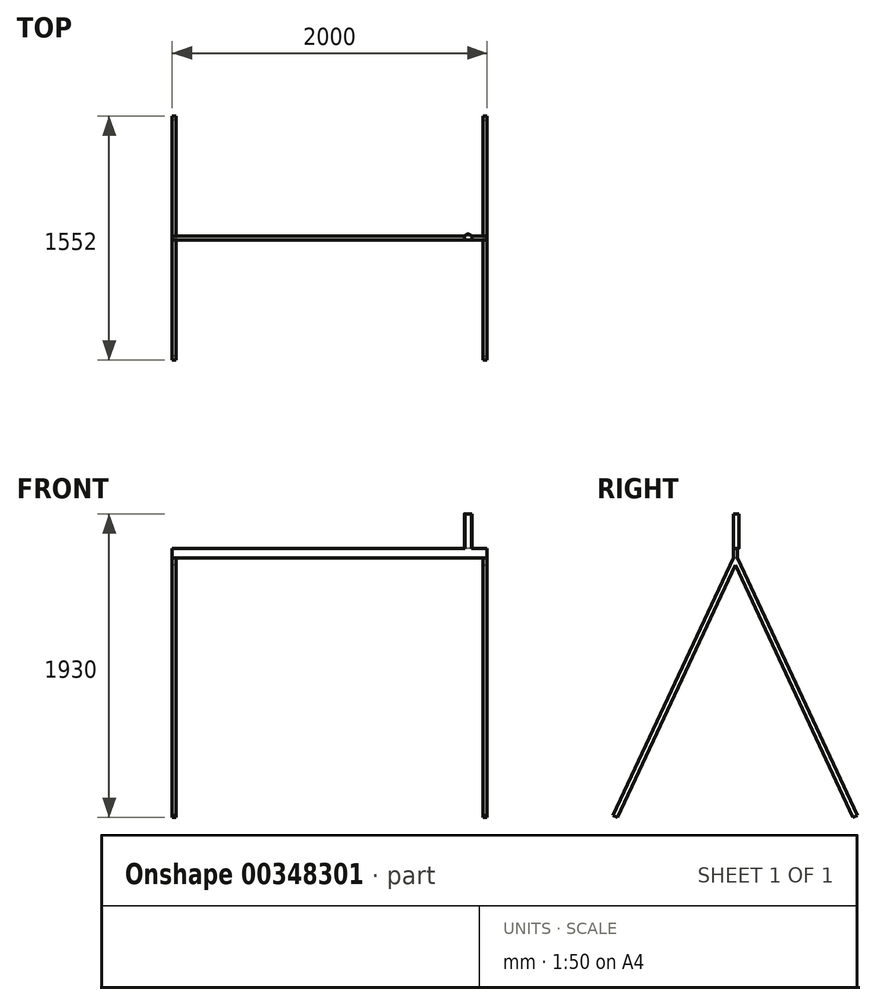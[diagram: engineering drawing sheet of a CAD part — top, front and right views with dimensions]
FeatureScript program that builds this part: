
annotation { "Feature Type Name" : "Feature", "Feature Type Description" : "" }
export const myFeature = defineFeature(function(context is Context, id is Id, definition is map)
    precondition{}
    {
        {
            var Q0;
            Q0=qCreatedBy(makeId("Right.planeOp"),FACE);
            var sketch = newSketch(context, id + "F0", { "sketchPlane" : qUnion([Q0])});
            skLineSegment(sketch, "E0.bottom", {"start": v(12.5, 1710) * mm, "end": v(-12.5, 1710) * mm});
            skLineSegment(sketch, "E0.top", {"start": v(12.5, 1650) * mm, "end": v(-12.5, 1650) * mm});
            skLineSegment(sketch, "E0.left", {"start": v(12.5, 1710) * mm, "end": v(12.5, 1650) * mm});
            skLineSegment(sketch, "E0.right", {"start": v(-12.5, 1710) * mm, "end": v(-12.5, 1650) * mm});
            skPoint(sketch, "E0.middle", {"position": v(0, 1680) * mm});
            skSolve(sketch);
        }
        {
            var Q0;
            Q0 = qSketchRegion(id + "F0", true);
            extrude(context, id + "F1", {"entities" : qUnion([Q0]), "depth" : 2000 * mm, "symmetric" : true});
        }
        {
            var Q0;
            Q0=makeQuery(id+"F1.opExtrude","CAP_FACE",FACE,{"disambiguationData":[OSD([sQuery(id+"F0.wireOp",EDGE,"E0.bottom"),sQuery(id+"F0.wireOp",EDGE,"E0.top"),sQuery(id+"F0.wireOp",EDGE,"E0.left"),sQuery(id+"F0.wireOp",EDGE,"E0.right")])],"isStart":false});
            var sketch = newSketch(context, id + "F2", { "sketchPlane" : qUnion([Q0])});
            skLineSegment(sketch, "E1", {"start": v(-12.5, 1650) * mm, "end": v(12.5, 1650) * mm});
            skLineSegment(sketch, "E2", {"start": v(12.5, 1650) * mm, "end": v(776, 12.68) * mm});
            skLineSegment(sketch, "E3", {"start": v(776, 12.68) * mm, "end": v(748.8, 0) * mm});
            skLineSegment(sketch, "E4", {"start": v(748.8, 0) * mm, "end": v(0, 1605.82) * mm});
            skLineSegment(sketch, "E5", {"start": v(0, 1605.82) * mm, "end": v(-748.8, 0) * mm});
            skLineSegment(sketch, "E6", {"start": v(-748.8, 0) * mm, "end": v(-776, 12.68) * mm});
            skLineSegment(sketch, "E7", {"start": v(-776, 12.68) * mm, "end": v(-12.5, 1650) * mm});
            skSolve(sketch);
        }
        {
            var Q0;
            Q0 = qSketchRegion(id + "F2", true);
            extrude(context, id + "F3", {"entities" : qUnion([Q0]), "oppositeDirection" : true, "depth" : 25 * mm});
        }
        {
            var Q0;
            Q0=makeQuery(id+"F3.opExtrude","SWEPT_BODY",BODY,{"disambiguationData":[OSD([sQuery(id+"F2.wireOp",EDGE,"E1"),sQuery(id+"F2.wireOp",EDGE,"E2"),sQuery(id+"F2.wireOp",EDGE,"E3"),sQuery(id+"F2.wireOp",EDGE,"E4"),sQuery(id+"F2.wireOp",EDGE,"E5"),sQuery(id+"F2.wireOp",EDGE,"E6"),sQuery(id+"F2.wireOp",EDGE,"E7")])]});
            var Q1;
            Q1=qCreatedBy(makeId("Right.planeOp"),FACE);
            mirror(context, id + "F4", {"operationType" : NewBodyOperationType.ADD, "entities" : qUnion([Q0]), "mirrorPlane" : qUnion([Q1])});
        }
        {
            var Q0;
            Q0=makeQuery(id+"F1.opExtrude","SWEPT_FACE",FACE,{"disambiguationData":[OSD([sQuery(id+"F0.wireOp",EDGE,"E0.bottom")])]});
            var sketch = newSketch(context, id + "F5", { "sketchPlane" : qUnion([Q0])});
            skCircle(sketch, "E8", {"center": v(880, 0) * mm, "radius": 25 * mm});
            skSolve(sketch);
        }
        {
            var Q0;
            {var subQ0=sQuery(id+"F5.wireOp",EDGE,"E8");var subQ1=makeQuery(id+"F1.opExtrude","SWEPT_EDGE",EDGE,{"disambiguationData":[OSD([sQuery(id+"F0.wireOp",EDGE,"E0.bottom"),sQuery(id+"F0.wireOp",EDGE,"E0.left")])]});var subQ2=makeQuery(id+"F5.imprint","INTERSECT",VERTEX,{"disambiguationData":[OD(0.0)],"derivedFrom":[subQ1,subQ0]});Q0=makeQuery(id+"F5.imprint","IMPRINT",FACE,{"disambiguationData":[TD([[makeQuery(id+"F5.imprint","IMPRINT",EDGE,{"disambiguationData":[TD([[subQ2,1.0]])],"derivedFrom":subQ0}),1.0]])]});}
            var Q1;
            {var subQ0=sQuery(id+"F5.wireOp",EDGE,"E8");var subQ1=sQuery(id+"F0.wireOp",EDGE,"E0.bottom");var subQ2=makeQuery(id+"F1.opExtrude","SWEPT_EDGE",EDGE,{"disambiguationData":[OSD([subQ1,sQuery(id+"F0.wireOp",EDGE,"E0.left")])]});var subQ3=makeQuery(id+"F5.imprint","INTERSECT",VERTEX,{"disambiguationData":[OD(0.0)],"derivedFrom":[subQ2,subQ0]});Q1=makeQuery(id+"F5.imprint","IMPRINT",FACE,{"disambiguationData":[TD([[makeQuery(id+"F5.imprint","IMPRINT",EDGE,{"disambiguationData":[TD([[subQ3,-1.0]])],"derivedFrom":subQ0}),1.0]])]});}
            var Q2;
            {var subQ0=sQuery(id+"F5.wireOp",EDGE,"E8");var subQ1=makeQuery(id+"F1.opExtrude","SWEPT_EDGE",EDGE,{"disambiguationData":[OSD([sQuery(id+"F0.wireOp",EDGE,"E0.bottom"),sQuery(id+"F0.wireOp",EDGE,"E0.right")])]});var subQ2=makeQuery(id+"F5.imprint","INTERSECT",VERTEX,{"disambiguationData":[OD(0.0)],"derivedFrom":[subQ1,subQ0]});Q2=makeQuery(id+"F5.imprint","IMPRINT",FACE,{"disambiguationData":[TD([[makeQuery(id+"F5.imprint","IMPRINT",EDGE,{"disambiguationData":[TD([[subQ2,-1.0]])],"derivedFrom":subQ0}),1.0]])]});}
            var Q3;
            Q3=sQuery(id+"F5.wireOp",EDGE,"E8");
            extrude(context, id + "F6", {"entities" : qUnion([Q0, Q1, Q2]), "operationType" : NewBodyOperationType.ADD, "surfaceEntities" : qUnion([Q3]), "depth" : 220 * mm, "offsetDistance" : 25 * mm});
        }
    });
